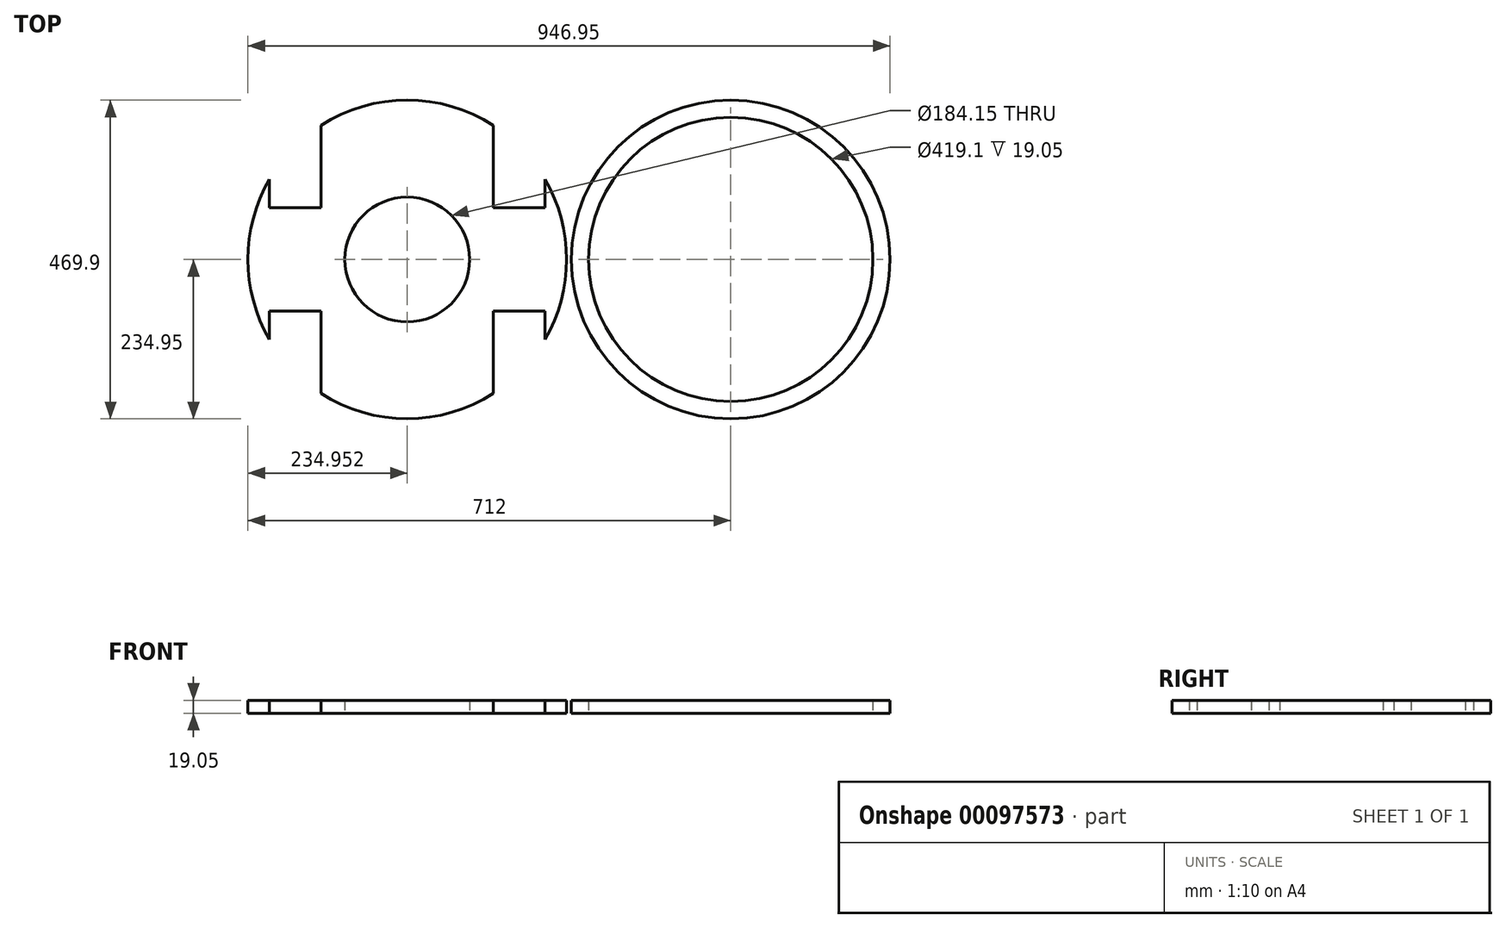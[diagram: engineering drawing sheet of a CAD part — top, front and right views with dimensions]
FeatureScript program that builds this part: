
annotation { "Feature Type Name" : "Feature", "Feature Type Description" : "" }
export const myFeature = defineFeature(function(context is Context, id is Id, definition is map)
    precondition{}
    {
        {
            var Q0;
            Q0=qCreatedBy(makeId("Top.planeOp"),FACE);
            var sketch = newSketch(context, id + "F0", { "sketchPlane" : qUnion([Q0])});
            skCircle(sketch, "E0", {"center": v(0, 0) * mm, "radius": 209.55 * mm});
            skCircle(sketch, "E1", {"center": v(0, 0) * mm, "radius": 234.95 * mm});
            skSolve(sketch);
        }
        {
            var Q0;
            Q0=makeQuery(id+"F0.imprint","IMPRINT",FACE,{"disambiguationData":[TD([[makeQuery(id+"F0.imprint","IMPRINT",EDGE,{"derivedFrom":sQuery(id+"F0.wireOp",EDGE,"E0")}),-1.0]])]});
            extrude(context, id + "F1", {"entities" : qUnion([Q0]), "depth" : 19.05 * mm, "offsetDistance" : 25.4 * mm});
        }
        {
            var Q0;
            Q0=qCreatedBy(makeId("Top.planeOp"),FACE);
            var sketch = newSketch(context, id + "F2", { "sketchPlane" : qUnion([Q0])});
            skArc(sketch, "E2", {"start": v(-350.05, 197.67) * mm, "mid": v(-477.05, 234.95) * mm, "end": v(-604.05, 197.67) * mm});
            skLineSegment(sketch, "E3.top", {"start": v(-680.25, 76.2) * mm, "end": v(-604.05, 76.2) * mm});
            skLineSegment(sketch, "E3.left", {"start": v(-680.25, 117.95) * mm, "end": v(-680.25, 76.2) * mm});
            skLineSegment(sketch, "E3.right", {"start": v(-604.05, 197.67) * mm, "end": v(-604.05, 76.2) * mm});
            skLineSegment(sketch, "E4", {"start": v(-477.05, 0) * mm, "end": v(-477.05, 275.95) * mm, "construction": true});
            skLineSegment(sketch, "E5.MirrorCS", {"start": v(-273.85, 117.95) * mm, "end": v(-273.85, 76.2) * mm});
            skLineSegment(sketch, "E6.MirrorCS", {"start": v(-350.05, 197.67) * mm, "end": v(-350.05, 76.2) * mm});
            skLineSegment(sketch, "E7.MirrorCS", {"start": v(-273.85, 76.2) * mm, "end": v(-350.05, 76.2) * mm});
            skLineSegment(sketch, "E8", {"start": v(-477.05, 0) * mm, "end": v(-368.05, 0) * mm, "construction": true});
            skLineSegment(sketch, "E9.MirrorCS", {"start": v(-273.85, -76.2) * mm, "end": v(-350.05, -76.2) * mm});
            skLineSegment(sketch, "E10.MirrorCS", {"start": v(-350.05, -197.67) * mm, "end": v(-350.05, -76.2) * mm});
            skLineSegment(sketch, "E11.MirrorCS", {"start": v(-273.85, -117.95) * mm, "end": v(-273.85, -76.2) * mm});
            skLineSegment(sketch, "E12.MirrorCS", {"start": v(-604.05, -197.67) * mm, "end": v(-604.05, -76.2) * mm});
            skLineSegment(sketch, "E13.MirrorCS", {"start": v(-680.25, -76.2) * mm, "end": v(-604.05, -76.2) * mm});
            skLineSegment(sketch, "E14.MirrorCS", {"start": v(-680.25, -117.95) * mm, "end": v(-680.25, -76.2) * mm});
            skPoint(sketch, "E15.MirrorCS.end.orphan", {"position": v(-350.05, 228.6) * mm});
            skPoint(sketch, "E15.MirrorCS.start.orphan", {"position": v(-273.85, 228.6) * mm});
            skPoint(sketch, "E16.orphan", {"position": v(-273.85, -228.6) * mm});
            skPoint(sketch, "E17.orphan", {"position": v(-350.05, -228.6) * mm});
            skArc(sketch, "E18.trimOffspring", {"start": v(-273.85, -117.95) * mm, "mid": v(-242.1, 0) * mm, "end": v(-273.85, 117.95) * mm});
            skPoint(sketch, "E19.orphan", {"position": v(-680.25, -228.6) * mm});
            skPoint(sketch, "E20.orphan", {"position": v(-604.05, -228.6) * mm});
            skArc(sketch, "E21.trimOffspring", {"start": v(-604.05, -197.67) * mm, "mid": v(-477.05, -234.95) * mm, "end": v(-350.05, -197.67) * mm});
            skPoint(sketch, "E22.orphan", {"position": v(-680.25, 228.6) * mm});
            skPoint(sketch, "E23.orphan", {"position": v(-604.05, 228.6) * mm});
            skArc(sketch, "E24.trimOffspring", {"start": v(-680.25, 117.95) * mm, "mid": v(-712, 0) * mm, "end": v(-680.25, -117.95) * mm});
            skCircle(sketch, "E25", {"center": v(-477.05, 0) * mm, "radius": 92.08 * mm});
            skSolve(sketch);
        }
        {
            var Q0;
            Q0=makeQuery(id+"F2.imprint","IMPRINT",FACE,{"disambiguationData":[TD([[makeQuery(id+"F2.imprint","IMPRINT",EDGE,{"derivedFrom":sQuery(id+"F2.wireOp",EDGE,"E2")}),1.0]])]});
            extrude(context, id + "F3", {"entities" : qUnion([Q0]), "depth" : 19.05 * mm, "offsetDistance" : 25.4 * mm});
        }
    });
